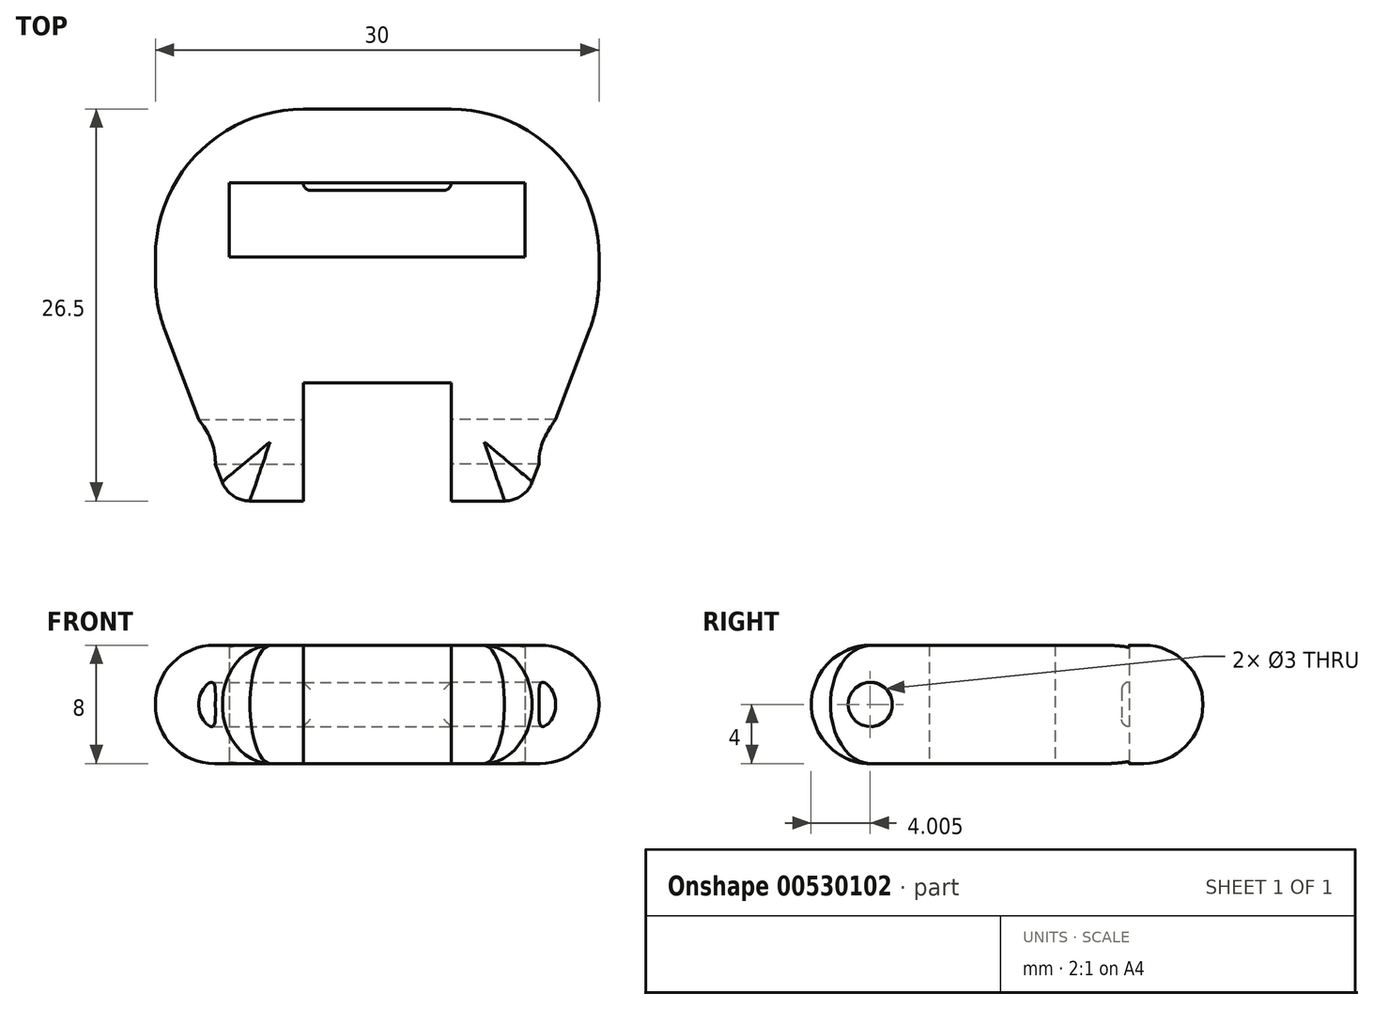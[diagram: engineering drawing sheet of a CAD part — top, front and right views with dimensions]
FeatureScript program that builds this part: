
annotation { "Feature Type Name" : "Feature", "Feature Type Description" : "" }
export const myFeature = defineFeature(function(context is Context, id is Id, definition is map)
    precondition{}
    {
        {
            var Q0;
            Q0=qCreatedBy(makeId("Top.planeOp"),FACE);
            var sketch = newSketch(context, id + "F0", { "sketchPlane" : qUnion([Q0])});
            skLineSegment(sketch, "E0.bottom", {"start": v(-27.64, 23.11) * mm, "end": v(2.36, 23.11) * mm});
            skLineSegment(sketch, "E0.top", {"start": v(-27.64, -3.39) * mm, "end": v(2.36, -3.39) * mm});
            skLineSegment(sketch, "E0.left", {"start": v(-27.64, 23.11) * mm, "end": v(-27.64, -3.39) * mm});
            skLineSegment(sketch, "E0.right", {"start": v(2.36, 23.11) * mm, "end": v(2.36, -3.39) * mm});
            skLineSegment(sketch, "E1.bottom", {"start": v(-22.64, 18.11) * mm, "end": v(-2.64, 18.11) * mm});
            skLineSegment(sketch, "E1.top", {"start": v(-22.64, 13.11) * mm, "end": v(-2.64, 13.11) * mm});
            skLineSegment(sketch, "E1.left", {"start": v(-22.64, 18.11) * mm, "end": v(-22.64, 13.11) * mm});
            skLineSegment(sketch, "E1.right", {"start": v(-2.64, 18.11) * mm, "end": v(-2.64, 13.11) * mm});
            skLineSegment(sketch, "E2.bottom", {"start": v(-17.64, 4.61) * mm, "end": v(-7.64, 4.61) * mm});
            skLineSegment(sketch, "E2.top", {"start": v(-17.64, -3.39) * mm, "end": v(-7.64, -3.39) * mm});
            skLineSegment(sketch, "E2.left", {"start": v(-17.64, 4.61) * mm, "end": v(-17.64, -3.39) * mm});
            skLineSegment(sketch, "E2.right", {"start": v(-7.64, 4.61) * mm, "end": v(-7.64, -3.39) * mm});
            skPoint(sketch, "E3", {"position": v(2.36, 9.86) * mm});
            skPoint(sketch, "E4", {"position": v(-27.64, 9.86) * mm});
            skPoint(sketch, "E5", {"position": v(-22.64, -3.39) * mm});
            skPoint(sketch, "E6", {"position": v(-2.64, -3.39) * mm});
            skLineSegment(sketch, "E7", {"start": v(-27.64, 9.86) * mm, "end": v(-22.64, -3.39) * mm});
            skLineSegment(sketch, "E8", {"start": v(2.36, 9.86) * mm, "end": v(-2.64, -3.39) * mm});
            skSolve(sketch);
        }
        {
            var Q0;
            Q0=makeQuery(id+"F0.imprint","IMPRINT",FACE,{"disambiguationData":[TD([[makeQuery(id+"F0.imprint","IMPRINT",EDGE,{"derivedFrom":sQuery(id+"F0.wireOp",EDGE,"E0.bottom")}),-1.0]])]});
            extrude(context, id + "F1", {"entities" : qUnion([Q0]), "depth" : 8 * mm, "offsetDistance" : 25 * mm});
        }
        {
            var Q0;
            Q0=makeQuery(id+"F1.opExtrude","SWEPT_EDGE",EDGE,{"disambiguationData":[OSD([sQuery(id+"F0.wireOp",EDGE,"E0.left"),sQuery(id+"F0.wireOp",EDGE,"E7")])]});
            var Q1;
            Q1=makeQuery(id+"F1.opExtrude","SWEPT_EDGE",EDGE,{"disambiguationData":[OSD([sQuery(id+"F0.wireOp",EDGE,"E0.right"),sQuery(id+"F0.wireOp",EDGE,"E8")])]});
            var Q2;
            Q2=makeQuery(id+"F1.opExtrude","SWEPT_EDGE",EDGE,{"disambiguationData":[OSD([sQuery(id+"F0.wireOp",EDGE,"E0.bottom"),sQuery(id+"F0.wireOp",EDGE,"E0.right")])]});
            var Q3;
            Q3=makeQuery(id+"F1.opExtrude","SWEPT_EDGE",EDGE,{"disambiguationData":[OSD([sQuery(id+"F0.wireOp",EDGE,"E0.bottom"),sQuery(id+"F0.wireOp",EDGE,"E0.left")])]});
            fillet(context, id + "F2", {"entities" : qUnion([Q0, Q1, Q2, Q3]), "radius" : 10 * mm, "tangentPropagation" : true, "allowEdgeOverflow" : false});
        }
        {
            var Q0;
            Q0=makeQuery(id+"F1.opExtrude","SWEPT_EDGE",EDGE,{"disambiguationData":[OSD([sQuery(id+"F0.wireOp",EDGE,"E0.top"),sQuery(id+"F0.wireOp",EDGE,"E7")])]});
            var Q1;
            Q1=makeQuery(id+"F1.opExtrude","SWEPT_EDGE",EDGE,{"disambiguationData":[OSD([sQuery(id+"F0.wireOp",EDGE,"E0.top"),sQuery(id+"F0.wireOp",EDGE,"E8")])]});
            fillet(context, id + "F3", {"entities" : qUnion([Q0, Q1]), "radius" : 2 * mm, "tangentPropagation" : true, "allowEdgeOverflow" : false});
        }
        {
            var Q0;
            {var subQ0=sQuery(id+"F0.wireOp",EDGE,"E0.top");Q0=makeQuery(id+"F1.opExtrude","CAP_EDGE",EDGE,{"disambiguationData":[OSD([subQ0]),TDD([makeQuery(id+"F0.imprint","IMPRINT",EDGE,{"disambiguationData":[TD([[makeQuery(id+"F0.imprint","INTERSECT",VERTEX,{"derivedFrom":[subQ0,sQuery(id+"F0.wireOp",EDGE,"E8")]}),1.0]])],"derivedFrom":subQ0})])],"isStart":true});}
            var Q1;
            {var subQ0=sQuery(id+"F0.wireOp",EDGE,"E0.top");Q1=makeQuery(id+"F1.opExtrude","CAP_EDGE",EDGE,{"disambiguationData":[OSD([subQ0]),TDD([makeQuery(id+"F0.imprint","IMPRINT",EDGE,{"disambiguationData":[TD([[makeQuery(id+"F0.imprint","INTERSECT",VERTEX,{"derivedFrom":[subQ0,sQuery(id+"F0.wireOp",EDGE,"E8")]}),1.0]])],"derivedFrom":subQ0})])],"isStart":false});}
            fillet(context, id + "F4", {"entities" : qUnion([Q0, Q1]), "radius" : 4 * mm, "tangentPropagation" : true, "allowEdgeOverflow" : false});
        }
        {
            var Q0;
            Q0=makeQuery(id+"F1.opExtrude","SWEPT_FACE",FACE,{"disambiguationData":[OSD([sQuery(id+"F0.wireOp",EDGE,"E1.bottom")])]});
            var sketch = newSketch(context, id + "F5", { "sketchPlane" : qUnion([Q0])});
            skLineSegment(sketch, "E9.bottom", {"start": v(-17.64, 5.5) * mm, "end": v(-7.64, 5.5) * mm});
            skLineSegment(sketch, "E9.top", {"start": v(-17.64, 2.5) * mm, "end": v(-7.64, 2.5) * mm});
            skLineSegment(sketch, "E9.left", {"start": v(-17.64, 5.5) * mm, "end": v(-17.64, 2.5) * mm});
            skLineSegment(sketch, "E9.right", {"start": v(-7.64, 5.5) * mm, "end": v(-7.64, 2.5) * mm});
            skSolve(sketch);
        }
        {
            var Q0;
            Q0=makeQuery(id+"F5.imprint","IMPRINT",FACE,{"disambiguationData":[TD([[makeQuery(id+"F5.imprint","IMPRINT",EDGE,{"derivedFrom":sQuery(id+"F5.wireOp",EDGE,"E9.bottom")}),-1.0]])]});
            extrude(context, id + "F6", {"entities" : qUnion([Q0]), "operationType" : NewBodyOperationType.ADD, "depth" : 0.5 * mm, "offsetDistance" : 25 * mm});
        }
        {
            var Q0;
            Q0=makeQuery(id+"F6.opExtrude","CAP_FACE",FACE,{"disambiguationData":[OSD([sQuery(id+"F5.wireOp",EDGE,"E9.bottom"),sQuery(id+"F5.wireOp",EDGE,"E9.top"),sQuery(id+"F5.wireOp",EDGE,"E9.left"),sQuery(id+"F5.wireOp",EDGE,"E9.right")])],"isStart":false});
            fillet(context, id + "F7", {"entities" : qUnion([Q0]), "radius" : 0.5 * mm, "tangentPropagation" : true, "allowEdgeOverflow" : false});
        }
        {
            var Q0;
            Q0=makeQuery(id+"F1.opExtrude","SWEPT_FACE",FACE,{"disambiguationData":[OSD([sQuery(id+"F0.wireOp",EDGE,"E2.left")])]});
            var sketch = newSketch(context, id + "F8", { "sketchPlane" : qUnion([Q0])});
            skCircle(sketch, "E10", {"center": v(0.61, 4) * mm, "radius": 1.5 * mm});
            skSolve(sketch);
        }
        {
            var Q0;
            Q0=makeQuery(id+"F1.opExtrude","SWEPT_FACE",FACE,{"disambiguationData":[OSD([sQuery(id+"F0.wireOp",EDGE,"E2.right")])]});
            var sketch = newSketch(context, id + "F9", { "sketchPlane" : qUnion([Q0])});
            skCircle(sketch, "E11", {"center": v(-0.61, 4) * mm, "radius": 1.5 * mm});
            skSolve(sketch);
        }
        {
            var Q0;
            Q0=makeQuery(id+"F8.imprint","IMPRINT",FACE,{"disambiguationData":[TD([[makeQuery(id+"F8.imprint","IMPRINT",EDGE,{"derivedFrom":sQuery(id+"F8.wireOp",EDGE,"E10")}),1.0]])]});
            extrude(context, id + "F10", {"entities" : qUnion([Q0]), "operationType" : NewBodyOperationType.REMOVE, "oppositeDirection" : true, "depth" : 25 * mm, "offsetDistance" : 25 * mm});
        }
        {
            var Q0;
            Q0=makeQuery(id+"F9.imprint","IMPRINT",FACE,{"disambiguationData":[TD([[makeQuery(id+"F9.imprint","IMPRINT",EDGE,{"derivedFrom":sQuery(id+"F9.wireOp",EDGE,"E11")}),1.0]])]});
            extrude(context, id + "F11", {"entities" : qUnion([Q0]), "operationType" : NewBodyOperationType.REMOVE, "oppositeDirection" : true, "depth" : 25 * mm, "offsetDistance" : 25 * mm});
        }
    });
